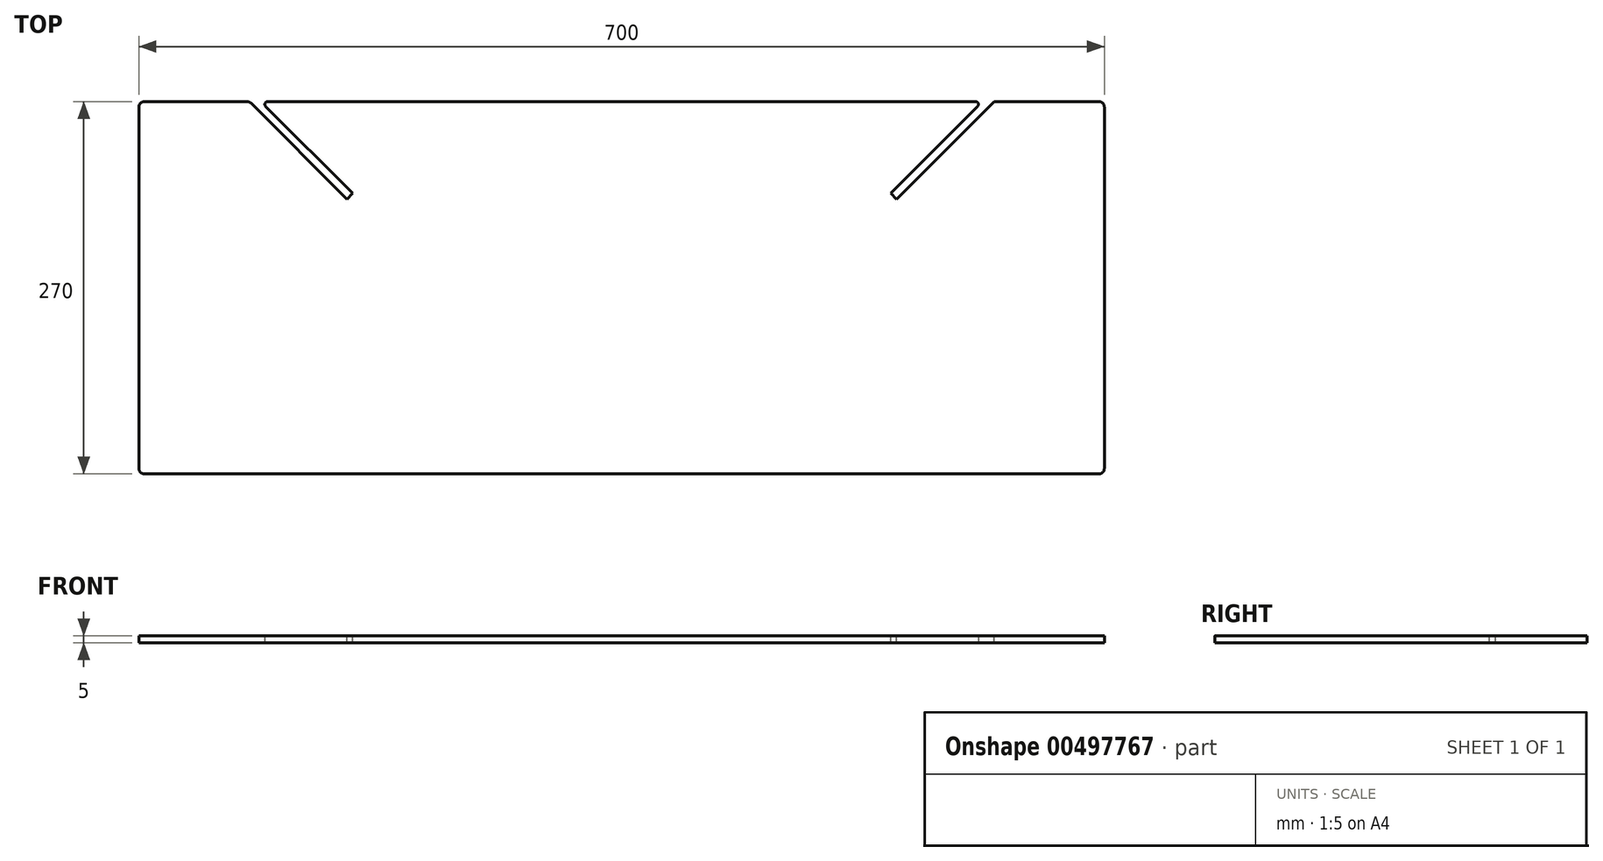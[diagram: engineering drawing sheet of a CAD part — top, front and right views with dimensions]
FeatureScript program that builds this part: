
annotation { "Feature Type Name" : "Feature", "Feature Type Description" : "" }
export const myFeature = defineFeature(function(context is Context, id is Id, definition is map)
    precondition{}
    {
        {
            var Q0;
            Q0=qCreatedBy(makeId("Top.planeOp"),FACE);
            var sketch = newSketch(context, id + "F0", { "sketchPlane" : qUnion([Q0])});
            skLineSegment(sketch, "E0.bottom", {"start": v(350, -135) * mm, "end": v(-350, -135) * mm});
            skLineSegment(sketch, "E0.top", {"start": v(350, 135) * mm, "end": v(-350, 135) * mm});
            skLineSegment(sketch, "E0.left", {"start": v(350, -135) * mm, "end": v(350, 135) * mm});
            skLineSegment(sketch, "E0.right", {"start": v(-350, -135) * mm, "end": v(-350, 135) * mm});
            skPoint(sketch, "E0.middle", {"position": v(0, 0) * mm});
            skSolve(sketch);
        }
        {
            var Q0;
            Q0 = qSketchRegion(id + "F0", true);
            extrude(context, id + "F1", {"entities" : qUnion([Q0]), "depth" : 5 * mm});
        }
        {
            var Q0;
            Q0=makeQuery(id+"F1.opExtrude","CAP_FACE",FACE,{"disambiguationData":[OSD([sQuery(id+"F0.wireOp",EDGE,"E0.bottom"),sQuery(id+"F0.wireOp",EDGE,"E0.top"),sQuery(id+"F0.wireOp",EDGE,"E0.left"),sQuery(id+"F0.wireOp",EDGE,"E0.right")])],"isStart":false});
            var sketch = newSketch(context, id + "F2", { "sketchPlane" : qUnion([Q0])});
            skLineSegment(sketch, "E1", {"start": v(0, -126.51) * mm, "end": v(261.51, 135) * mm, "construction": true});
            skPoint(sketch, "E1.startSnap0", {"position": v(0, -135) * mm});
            skLineSegment(sketch, "E2", {"start": v(261.51, 135) * mm, "end": v(270, 135) * mm, "construction": true});
            skLineSegment(sketch, "E3", {"start": v(270, 135) * mm, "end": v(0, -135) * mm, "construction": true});
            skLineSegment(sketch, "E4", {"start": v(0, -126.51) * mm, "end": v(-261.51, 135) * mm, "construction": true});
            skLineSegment(sketch, "E5", {"start": v(-261.51, 135) * mm, "end": v(-270, 135) * mm, "construction": true});
            skLineSegment(sketch, "E6", {"start": v(-270, 135) * mm, "end": v(0, -135) * mm, "construction": true});
            skLineSegment(sketch, "E7", {"start": v(-270, 135) * mm, "end": v(-261.51, 135) * mm});
            skLineSegment(sketch, "E8", {"start": v(-261.51, 135) * mm, "end": v(-195.05, 68.53) * mm});
            skLineSegment(sketch, "E9", {"start": v(-195.05, 68.53) * mm, "end": v(-199.29, 64.29) * mm});
            skLineSegment(sketch, "E10", {"start": v(-199.29, 64.29) * mm, "end": v(-270, 135) * mm});
            skLineSegment(sketch, "E11", {"start": v(261.51, 135) * mm, "end": v(270, 135) * mm});
            skLineSegment(sketch, "E12", {"start": v(199.29, 64.29) * mm, "end": v(270, 135) * mm});
            skLineSegment(sketch, "E13", {"start": v(199.29, 64.29) * mm, "end": v(195.05, 68.53) * mm});
            skLineSegment(sketch, "E14", {"start": v(195.05, 68.53) * mm, "end": v(261.51, 135) * mm});
            skLineSegment(sketch, "E15", {"start": v(-270, 135) * mm, "end": v(-286.97, 151.97) * mm, "construction": true});
            skLineSegment(sketch, "E16", {"start": v(-286.97, 151.97) * mm, "end": v(-282.73, 156.21) * mm, "construction": true});
            skLineSegment(sketch, "E17", {"start": v(-282.73, 156.21) * mm, "end": v(-261.51, 135) * mm, "construction": true});
            skSolve(sketch);
        }
        {
            var Q0;
            Q0 = qSketchRegion(id + "F2", true);
            extrude(context, id + "F3", {"entities" : qUnion([Q0]), "operationType" : NewBodyOperationType.REMOVE, "oppositeDirection" : true, "depth" : 25 * mm});
        }
        {
            var Q0;
            Q0=makeQuery(id+"F1.opExtrude","SWEPT_EDGE",EDGE,{"disambiguationData":[OSD([sQuery(id+"F0.wireOp",EDGE,"E0.bottom"),sQuery(id+"F0.wireOp",EDGE,"E0.right")])]});
            var Q1;
            Q1=makeQuery(id+"F1.opExtrude","SWEPT_EDGE",EDGE,{"disambiguationData":[OSD([sQuery(id+"F0.wireOp",EDGE,"E0.bottom"),sQuery(id+"F0.wireOp",EDGE,"E0.left")])]});
            var Q2;
            Q2=makeQuery(id+"F1.opExtrude","SWEPT_EDGE",EDGE,{"disambiguationData":[OSD([sQuery(id+"F0.wireOp",EDGE,"E0.top"),sQuery(id+"F0.wireOp",EDGE,"E0.left")])]});
            var Q3;
            Q3=makeQuery(id+"F1.opExtrude","SWEPT_EDGE",EDGE,{"disambiguationData":[OSD([sQuery(id+"F0.wireOp",EDGE,"E0.top"),sQuery(id+"F0.wireOp",EDGE,"E0.right")])]});
            var Q4;
            Q4=makeQuery(id+"F3.boolean.opBoolean","COPY",EDGE,{"derivedFrom":makeQuery(id+"F3.opExtrude","SWEPT_EDGE",EDGE,{"disambiguationData":[OSD([sQuery(id+"F0.wireOp",EDGE,"E0.top"),sQuery(id+"F2.wireOp",EDGE,"E7"),sQuery(id+"F2.wireOp",EDGE,"E10")])]})});
            var Q5;
            Q5=makeQuery(id+"F3.boolean.opBoolean","COPY",EDGE,{"derivedFrom":makeQuery(id+"F3.opExtrude","SWEPT_EDGE",EDGE,{"disambiguationData":[OSD([sQuery(id+"F0.wireOp",EDGE,"E0.top"),sQuery(id+"F2.wireOp",EDGE,"E11"),sQuery(id+"F2.wireOp",EDGE,"E12")])]})});
            fillet(context, id + "F4", {"entities" : qUnion([Q0, Q1, Q2, Q3, Q4, Q5]), "radius" : 4 * mm, "tangentPropagation" : true, "allowEdgeOverflow" : false});
        }
        {
            var Q0;
            Q0=makeQuery(id+"F3.boolean.opBoolean","COPY",EDGE,{"derivedFrom":makeQuery(id+"F3.opExtrude","SWEPT_EDGE",EDGE,{"disambiguationData":[OSD([sQuery(id+"F0.wireOp",EDGE,"E0.top"),sQuery(id+"F2.wireOp",EDGE,"E11"),sQuery(id+"F2.wireOp",EDGE,"E14")])]})});
            var Q1;
            Q1=makeQuery(id+"F3.boolean.opBoolean","COPY",EDGE,{"derivedFrom":makeQuery(id+"F3.opExtrude","SWEPT_EDGE",EDGE,{"disambiguationData":[OSD([sQuery(id+"F0.wireOp",EDGE,"E0.top"),sQuery(id+"F2.wireOp",EDGE,"E7"),sQuery(id+"F2.wireOp",EDGE,"E8")])]})});
            fillet(context, id + "F5", {"entities" : qUnion([Q0, Q1]), "radius" : 2 * mm, "tangentPropagation" : true, "allowEdgeOverflow" : false});
        }
    });
